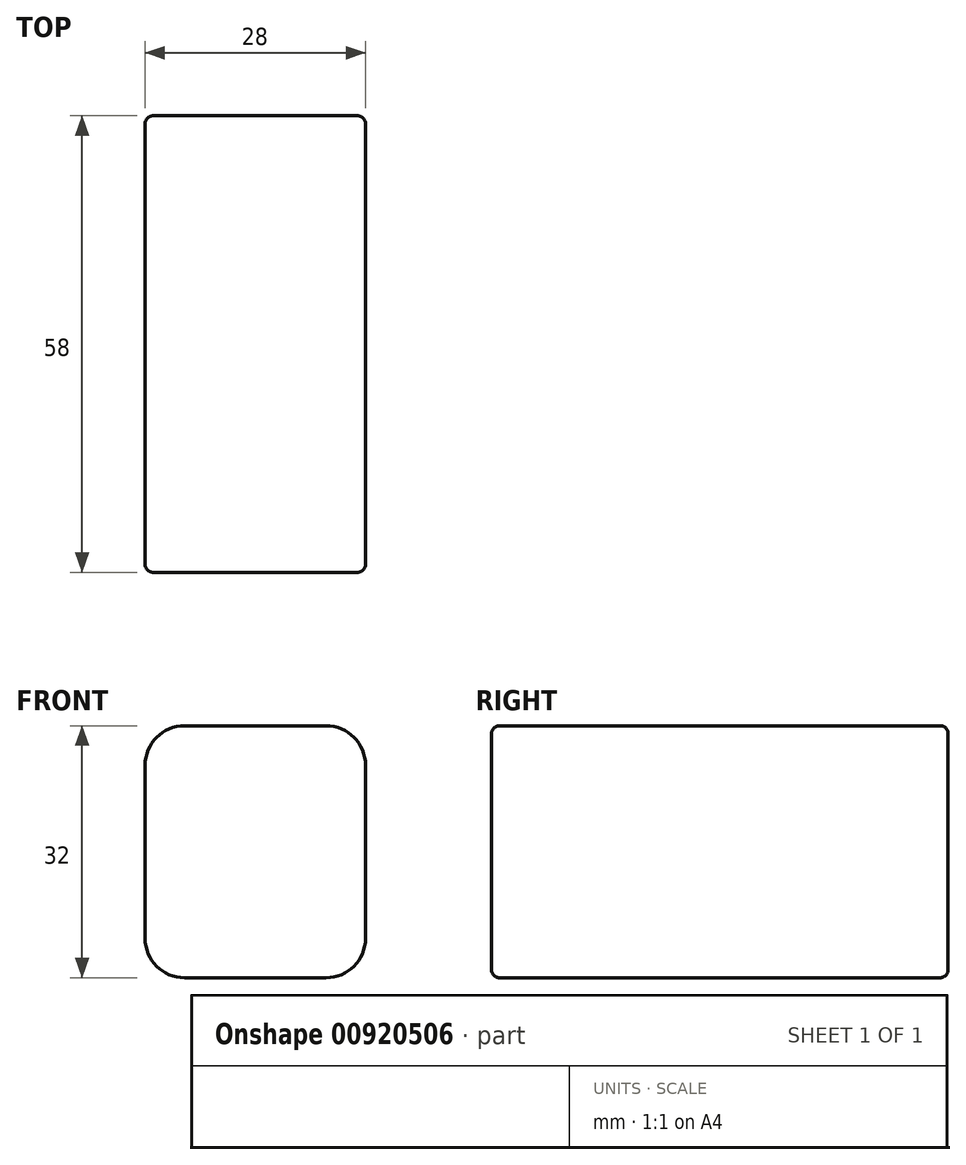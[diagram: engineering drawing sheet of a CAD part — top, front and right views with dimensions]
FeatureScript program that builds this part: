
annotation { "Feature Type Name" : "Feature", "Feature Type Description" : "" }
export const myFeature = defineFeature(function(context is Context, id is Id, definition is map)
    precondition{}
    {
        {
            var Q0;
            Q0=qCreatedBy(makeId("Front.planeOp"),FACE);
            var sketch = newSketch(context, id + "F0", { "sketchPlane" : qUnion([Q0])});
            skLineSegment(sketch, "E0.bottom", {"start": v(-14, 16) * mm, "end": v(14, 16) * mm});
            skLineSegment(sketch, "E0.top", {"start": v(-14, -16) * mm, "end": v(14, -16) * mm});
            skLineSegment(sketch, "E0.left", {"start": v(-14, 16) * mm, "end": v(-14, -16) * mm});
            skLineSegment(sketch, "E0.right", {"start": v(14, 16) * mm, "end": v(14, -16) * mm});
            skSolve(sketch);
        }
        {
            var Q0;
            Q0=makeQuery(id+"F0.imprint","IMPRINT",FACE,{"disambiguationData":[TD([[makeQuery(id+"F0.imprint","IMPRINT",EDGE,{"derivedFrom":sQuery(id+"F0.wireOp",EDGE,"E0.bottom")}),-1.0]])]});
            extrude(context, id + "F1", {"entities" : qUnion([Q0]), "depth" : 58 * mm, "offsetDistance" : 25 * mm});
        }
        {
            var Q0;
            Q0=makeQuery(id+"F1.opExtrude","CAP_EDGE",EDGE,{"disambiguationData":[OSD([sQuery(id+"F0.wireOp",EDGE,"E0.bottom")])],"isStart":false});
            var Q1;
            Q1=makeQuery(id+"F1.opExtrude","CAP_EDGE",EDGE,{"disambiguationData":[OSD([sQuery(id+"F0.wireOp",EDGE,"E0.right")])],"isStart":false});
            var Q2;
            Q2=makeQuery(id+"F1.opExtrude","CAP_EDGE",EDGE,{"disambiguationData":[OSD([sQuery(id+"F0.wireOp",EDGE,"E0.top")])],"isStart":false});
            var Q3;
            Q3=makeQuery(id+"F1.opExtrude","CAP_EDGE",EDGE,{"disambiguationData":[OSD([sQuery(id+"F0.wireOp",EDGE,"E0.left")])],"isStart":false});
            var Q4;
            Q4=makeQuery(id+"F1.opExtrude","CAP_EDGE",EDGE,{"disambiguationData":[OSD([sQuery(id+"F0.wireOp",EDGE,"E0.right")])],"isStart":true});
            var Q5;
            Q5=makeQuery(id+"F1.opExtrude","CAP_EDGE",EDGE,{"disambiguationData":[OSD([sQuery(id+"F0.wireOp",EDGE,"E0.bottom")])],"isStart":true});
            var Q6;
            Q6=makeQuery(id+"F1.opExtrude","CAP_EDGE",EDGE,{"disambiguationData":[OSD([sQuery(id+"F0.wireOp",EDGE,"E0.top")])],"isStart":true});
            var Q7;
            Q7=makeQuery(id+"F1.opExtrude","CAP_EDGE",EDGE,{"disambiguationData":[OSD([sQuery(id+"F0.wireOp",EDGE,"E0.left")])],"isStart":true});
            fillet(context, id + "F2", {"entities" : qUnion([Q0, Q1, Q2, Q3, Q4, Q5, Q6, Q7]), "radius" : 1 * mm, "tangentPropagation" : true, "allowEdgeOverflow" : false});
        }
        {
            var Q0;
            Q0=makeQuery(id+"F1.opExtrude","SWEPT_EDGE",EDGE,{"disambiguationData":[OSD([sQuery(id+"F0.wireOp",EDGE,"E0.bottom"),sQuery(id+"F0.wireOp",EDGE,"E0.right")])]});
            var Q1;
            Q1=makeQuery(id+"F1.opExtrude","SWEPT_EDGE",EDGE,{"disambiguationData":[OSD([sQuery(id+"F0.wireOp",EDGE,"E0.bottom"),sQuery(id+"F0.wireOp",EDGE,"E0.left")])]});
            var Q2;
            Q2=makeQuery(id+"F1.opExtrude","SWEPT_EDGE",EDGE,{"disambiguationData":[OSD([sQuery(id+"F0.wireOp",EDGE,"E0.top"),sQuery(id+"F0.wireOp",EDGE,"E0.right")])]});
            var Q3;
            Q3=makeQuery(id+"F1.opExtrude","SWEPT_EDGE",EDGE,{"disambiguationData":[OSD([sQuery(id+"F0.wireOp",EDGE,"E0.top"),sQuery(id+"F0.wireOp",EDGE,"E0.left")])]});
            fillet(context, id + "F3", {"entities" : qUnion([Q0, Q1, Q2, Q3]), "radius" : 5 * mm, "tangentPropagation" : true, "allowEdgeOverflow" : false});
        }
    });
